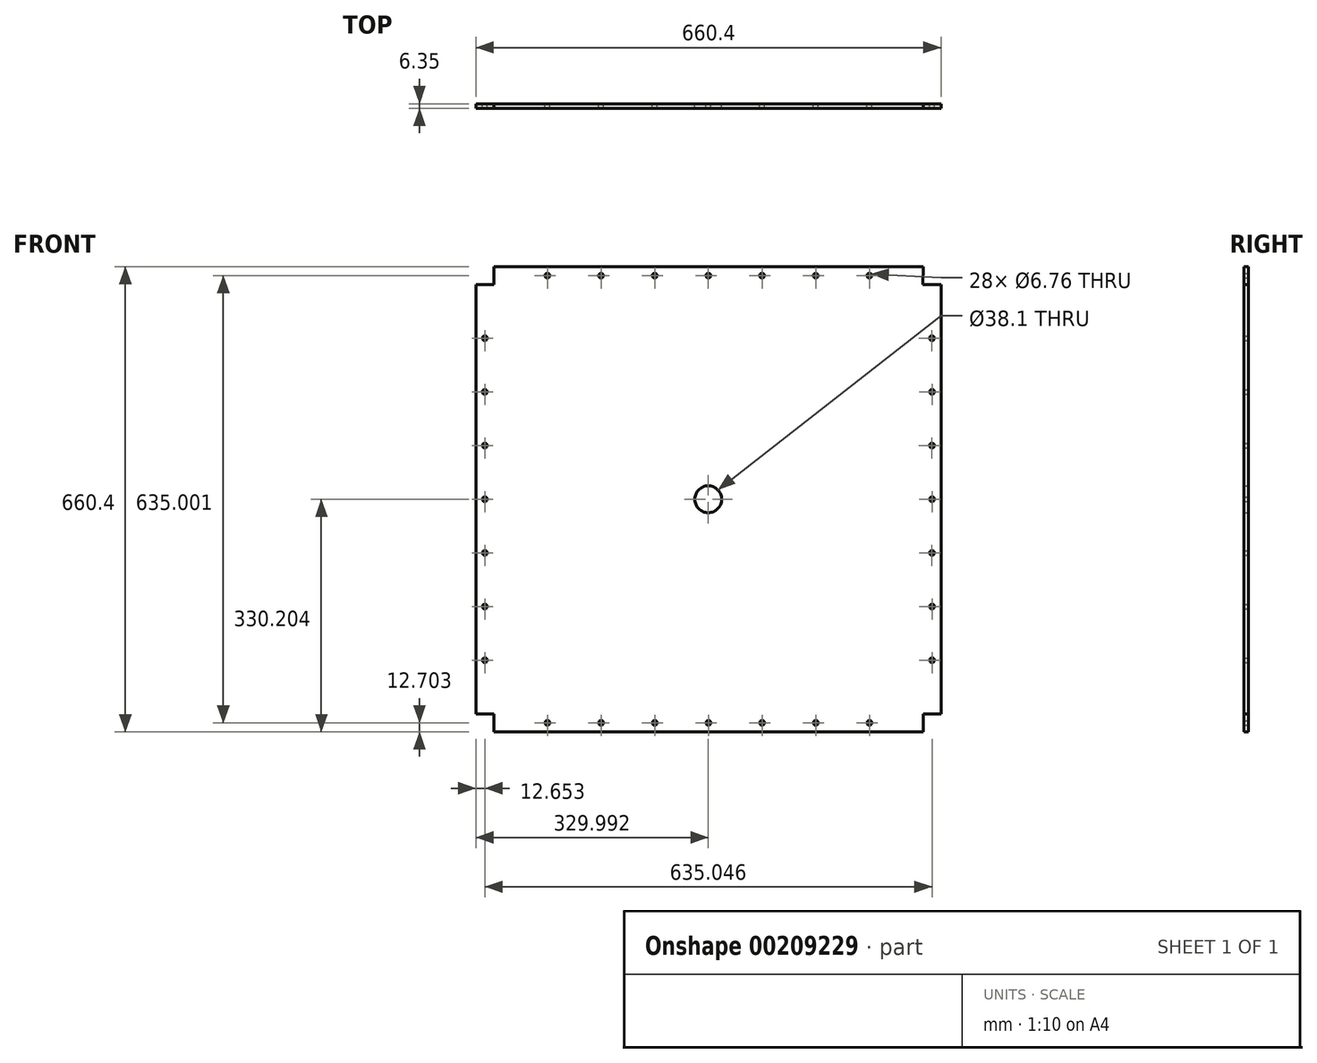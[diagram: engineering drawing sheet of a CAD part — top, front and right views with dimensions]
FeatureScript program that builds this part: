
annotation { "Feature Type Name" : "Feature", "Feature Type Description" : "" }
export const myFeature = defineFeature(function(context is Context, id is Id, definition is map)
    precondition{}
    {
        {
            var Q0;
            Q0=qCreatedBy(makeId("Front.planeOp"),FACE);
            var sketch = newSketch(context, id + "F0", { "sketchPlane" : qUnion([Q0])});
            skLineSegment(sketch, "E0.bottom", {"start": v(-553.57, 601.61) * mm, "end": v(56.03, 601.61) * mm});
            skLineSegment(sketch, "E0.top", {"start": v(-553.57, -58.79) * mm, "end": v(56.03, -58.79) * mm});
            skLineSegment(sketch, "E0.left", {"start": v(-578.97, 576.21) * mm, "end": v(-578.97, -33.39) * mm});
            skLineSegment(sketch, "E0.right", {"start": v(81.43, 576.21) * mm, "end": v(81.43, -33.44) * mm});
            skPoint(sketch, "E1", {"position": v(-578.97, 576.21) * mm});
            skPoint(sketch, "E2", {"position": v(-578.97, -33.39) * mm});
            skPoint(sketch, "E3", {"position": v(-553.57, 601.61) * mm});
            skPoint(sketch, "E4", {"position": v(56.03, 601.61) * mm});
            skPoint(sketch, "E5", {"position": v(81.43, 576.21) * mm});
            skPoint(sketch, "E6", {"position": v(81.43, -33.44) * mm});
            skPoint(sketch, "E7", {"position": v(56.03, -58.79) * mm});
            skPoint(sketch, "E8", {"position": v(-553.57, -58.79) * mm});
            skPoint(sketch, "E9", {"position": v(55.71, 576.21) * mm});
            skPoint(sketch, "E10", {"position": v(56.03, -33.44) * mm});
            skPoint(sketch, "E11", {"position": v(-553.53, -33.39) * mm});
            skLineSegment(sketch, "E12", {"start": v(-578.97, -33.39) * mm, "end": v(-553.53, -33.39) * mm});
            skLineSegment(sketch, "E13", {"start": v(-553.53, -33.39) * mm, "end": v(-553.57, -58.79) * mm});
            skLineSegment(sketch, "E14", {"start": v(81.43, -33.44) * mm, "end": v(56.03, -33.44) * mm});
            skLineSegment(sketch, "E15", {"start": v(56.03, -33.39) * mm, "end": v(56.03, -58.79) * mm});
            skLineSegment(sketch, "E16", {"start": v(56.03, 601.61) * mm, "end": v(55.71, 576.21) * mm});
            skLineSegment(sketch, "E17", {"start": v(55.71, 576.21) * mm, "end": v(81.43, 576.21) * mm});
            skPoint(sketch, "E18.orphan", {"position": v(-578.97, 601.61) * mm});
            skPoint(sketch, "E19.orphan", {"position": v(81.43, 601.61) * mm});
            skPoint(sketch, "E20.orphan", {"position": v(81.43, -58.79) * mm});
            skPoint(sketch, "E21.orphan", {"position": v(-578.97, -58.79) * mm});
            skPoint(sketch, "E22", {"position": v(-248.98, 271.41) * mm});
            skPoint(sketch, "E23", {"position": v(-248.77, 601.61) * mm});
            skPoint(sketch, "E24", {"position": v(-248.77, -58.79) * mm});
            skPoint(sketch, "E25", {"position": v(81.43, 271.39) * mm});
            skPoint(sketch, "E26", {"position": v(-578.97, 271.41) * mm});
            skPoint(sketch, "E27", {"position": v(68.73, 271.41) * mm});
            skPoint(sketch, "E28", {"position": v(-578.97, 423.81) * mm});
            skPoint(sketch, "E29", {"position": v(-578.97, 119.01) * mm});
            skPoint(sketch, "E30", {"position": v(-401.17, -58.79) * mm});
            skPoint(sketch, "E31", {"position": v(-96.37, -58.79) * mm});
            skPoint(sketch, "E32", {"position": v(81.43, 118.96) * mm});
            skPoint(sketch, "E33", {"position": v(81.43, 423.81) * mm});
            skPoint(sketch, "E34", {"position": v(-96.37, 601.61) * mm});
            skPoint(sketch, "E35", {"position": v(-401.17, 601.61) * mm});
            skPoint(sketch, "E36", {"position": v(-566.32, 423.81) * mm});
            skPoint(sketch, "E37", {"position": v(-566.27, 119.01) * mm});
            skPoint(sketch, "E38", {"position": v(-401.16, -46.09) * mm});
            skPoint(sketch, "E39", {"position": v(-96.36, -46.09) * mm});
            skPoint(sketch, "E40", {"position": v(68.73, 119.01) * mm});
            skPoint(sketch, "E41", {"position": v(68.73, 423.81) * mm});
            skPoint(sketch, "E42", {"position": v(-401.25, 588.86) * mm});
            skPoint(sketch, "E43", {"position": v(-96.45, 588.86) * mm});
            skPoint(sketch, "E44", {"position": v(-553.57, 576.21) * mm});
            skLineSegment(sketch, "E45", {"start": v(-578.97, 576.21) * mm, "end": v(-553.57, 576.21) * mm});
            skLineSegment(sketch, "E46", {"start": v(-553.57, 576.21) * mm, "end": v(-553.57, 601.61) * mm});
            skLineSegment(sketch, "E47", {"start": v(-578.97, 601.61) * mm, "end": v(81.43, -58.79) * mm, "construction": true});
            skLineSegment(sketch, "E48", {"start": v(-578.97, -58.79) * mm, "end": v(81.43, 601.61) * mm, "construction": true});
            skPoint(sketch, "E49", {"position": v(-566.27, 576.21) * mm});
            skPoint(sketch, "E50", {"position": v(-553.57, 588.91) * mm});
            skPoint(sketch, "E51", {"position": v(55.87, 588.91) * mm});
            skPoint(sketch, "E52", {"position": v(68.57, 576.21) * mm});
            skLineSegment(sketch, "E53", {"start": v(-553.57, 588.91) * mm, "end": v(55.87, 588.91) * mm, "construction": true});
            skPoint(sketch, "E54", {"position": v(-553.57, -46.09) * mm});
            skPoint(sketch, "E54.positionSnap0", {"position": v(-553.55, -46.09) * mm});
            skPoint(sketch, "E55", {"position": v(-566.25, -33.39) * mm});
            skPoint(sketch, "E56", {"position": v(56.03, -46.09) * mm});
            skPoint(sketch, "E57", {"position": v(68.73, -33.44) * mm});
            skPoint(sketch, "E58", {"position": v(148.6, 313.7) * mm});
            skLineSegment(sketch, "E59", {"start": v(-566.27, 576.21) * mm, "end": v(-566.25, -33.39) * mm, "construction": true});
            skLineSegment(sketch, "E60", {"start": v(-553.55, -46.09) * mm, "end": v(56.03, -46.09) * mm, "construction": true});
            skLineSegment(sketch, "E61", {"start": v(68.73, -33.44) * mm, "end": v(68.57, 576.21) * mm, "construction": true});
            skPoint(sketch, "E62", {"position": v(-325.05, 588.91) * mm});
            skPoint(sketch, "E63", {"position": v(-172.65, 588.91) * mm});
            skPoint(sketch, "E64", {"position": v(-20.25, 588.91) * mm});
            skPoint(sketch, "E65", {"position": v(-477.45, 588.91) * mm});
            skPoint(sketch, "E66", {"position": v(-248.85, 588.91) * mm});
            skPoint(sketch, "E67", {"position": v(-566.27, 500.01) * mm});
            skPoint(sketch, "E68", {"position": v(-566.26, 347.61) * mm});
            skPoint(sketch, "E69", {"position": v(-566.26, 195.21) * mm});
            skPoint(sketch, "E70", {"position": v(-566.25, 42.81) * mm});
            skPoint(sketch, "E71", {"position": v(-477.36, -46.09) * mm});
            skPoint(sketch, "E72", {"position": v(-324.96, -46.09) * mm});
            skPoint(sketch, "E73", {"position": v(-172.56, -46.09) * mm});
            skPoint(sketch, "E74", {"position": v(-20.16, -46.09) * mm});
            skPoint(sketch, "E75", {"position": v(68.7, 42.81) * mm});
            skPoint(sketch, "E76", {"position": v(68.67, 195.21) * mm});
            skPoint(sketch, "E77", {"position": v(68.63, 347.61) * mm});
            skPoint(sketch, "E78", {"position": v(68.6, 500.01) * mm});
            skPoint(sketch, "E79", {"position": v(-566.26, 271.41) * mm});
            skPoint(sketch, "E80", {"position": v(-248.76, -46.09) * mm});
            skCircle(sketch, "E81", {"center": v(-248.98, 271.41) * mm, "radius": 19.05 * mm});
            skSolve(sketch);
        }
        {
            var Q0;
            Q0=makeQuery(id+"F0.imprint","IMPRINT",FACE,{"disambiguationData":[TD([[makeQuery(id+"F0.imprint","IMPRINT",EDGE,{"derivedFrom":sQuery(id+"F0.wireOp",EDGE,"E0.bottom")}),-1.0]])]});
            extrude(context, id + "F1", {"entities" : qUnion([Q0]), "depth" : 6.35 * mm});
        }
        {
            var Q0;
            Q0=sQuery(id+"F0.wireOp",VERTEX,"E65");
            var Q1;
            Q1=sQuery(id+"F0.wireOp",VERTEX,"E42");
            var Q2;
            Q2=sQuery(id+"F0.wireOp",VERTEX,"E62");
            var Q3;
            Q3=sQuery(id+"F0.wireOp",VERTEX,"E66");
            var Q4;
            Q4=sQuery(id+"F0.wireOp",VERTEX,"E63");
            var Q5;
            Q5=sQuery(id+"F0.wireOp",VERTEX,"E43");
            var Q6;
            Q6=sQuery(id+"F0.wireOp",VERTEX,"E64");
            var Q7;
            Q7=sQuery(id+"F0.wireOp",VERTEX,"E78");
            var Q8;
            Q8=sQuery(id+"F0.wireOp",VERTEX,"E41");
            var Q9;
            Q9=sQuery(id+"F0.wireOp",VERTEX,"E77");
            var Q10;
            Q10=sQuery(id+"F0.wireOp",VERTEX,"E27");
            var Q11;
            Q11=sQuery(id+"F0.wireOp",VERTEX,"E76");
            var Q12;
            Q12=sQuery(id+"F0.wireOp",VERTEX,"E40");
            var Q13;
            Q13=sQuery(id+"F0.wireOp",VERTEX,"E75");
            var Q14;
            Q14=sQuery(id+"F0.wireOp",VERTEX,"E74");
            var Q15;
            Q15=sQuery(id+"F0.wireOp",VERTEX,"E39");
            var Q16;
            Q16=sQuery(id+"F0.wireOp",VERTEX,"E73");
            var Q17;
            Q17=sQuery(id+"F0.wireOp",VERTEX,"E80");
            var Q18;
            Q18=sQuery(id+"F0.wireOp",VERTEX,"E72");
            var Q19;
            Q19=sQuery(id+"F0.wireOp",VERTEX,"E38");
            var Q20;
            Q20=sQuery(id+"F0.wireOp",VERTEX,"E71");
            var Q21;
            Q21=sQuery(id+"F0.wireOp",VERTEX,"E70");
            var Q22;
            Q22=sQuery(id+"F0.wireOp",VERTEX,"E37");
            var Q23;
            Q23=sQuery(id+"F0.wireOp",VERTEX,"E69");
            var Q24;
            Q24=sQuery(id+"F0.wireOp",VERTEX,"E79");
            var Q25;
            Q25=sQuery(id+"F0.wireOp",VERTEX,"E68");
            var Q26;
            Q26=sQuery(id+"F0.wireOp",VERTEX,"E36");
            var Q27;
            Q27=sQuery(id+"F0.wireOp",VERTEX,"E67");
            var Q28;
            Q28=makeQuery(id+"F1.opExtrude","SWEPT_BODY",BODY,{"disambiguationData":[OSD([sQuery(id+"F0.wireOp",EDGE,"E0.bottom"),sQuery(id+"F0.wireOp",EDGE,"E0.top"),sQuery(id+"F0.wireOp",EDGE,"E0.left"),sQuery(id+"F0.wireOp",EDGE,"E0.right"),sQuery(id+"F0.wireOp",EDGE,"E12"),sQuery(id+"F0.wireOp",EDGE,"E13"),sQuery(id+"F0.wireOp",EDGE,"E14"),sQuery(id+"F0.wireOp",EDGE,"E15"),sQuery(id+"F0.wireOp",EDGE,"E16"),sQuery(id+"F0.wireOp",EDGE,"E17"),sQuery(id+"F0.wireOp",EDGE,"E45"),sQuery(id+"F0.wireOp",EDGE,"E46")])]});
            hole(context, id + "F2", {"style" : HoleStyle.SIMPLE, "endStyle" : HoleEndStyle.BLIND, "oppositeDirection" : true, "standardTappedOrClearance" : lookupTablePath({ "standard" : "ANSI", "fit" : "Normal (ASME)", "size" : "1/4", "type" : "Clearance" }), "standardBlindInLast" : lookupTablePath({ "fit" : "Free", "standard" : "ANSI", "size" : "1/4", "type" : "Clearance" }), "holeDiameter" : 6.76 * mm, "holeDepth" : 6.35 * mm, "locations" : qUnion([Q0, Q1, Q2, Q3, Q4, Q5, Q6, Q7, Q8, Q9, Q10, Q11, Q12, Q13, Q14, Q15, Q16, Q17, Q18, Q19, Q20, Q21, Q22, Q23, Q24, Q25, Q26, Q27]), "scope" : qUnion([Q28])});
        }
    });
